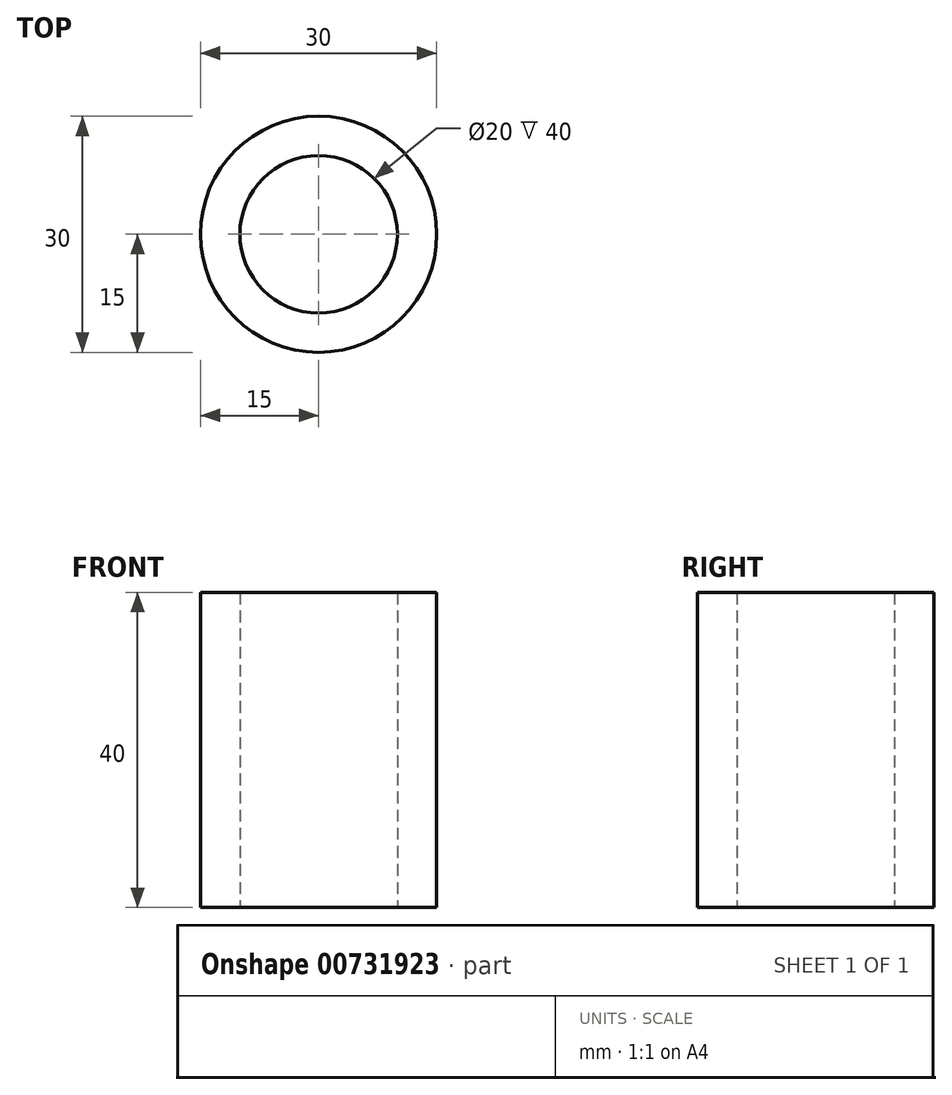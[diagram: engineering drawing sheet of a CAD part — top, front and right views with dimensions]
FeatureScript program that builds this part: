
annotation { "Feature Type Name" : "Feature", "Feature Type Description" : "" }
export const myFeature = defineFeature(function(context is Context, id is Id, definition is map)
    precondition{}
    {
        {
            var Q0;
            Q0=qCreatedBy(makeId("Top.planeOp"),FACE);
            var sketch = newSketch(context, id + "F0", { "sketchPlane" : qUnion([Q0])});
            skCircle(sketch, "E0", {"center": v(0, 0) * mm, "radius": 15 * mm});
            skCircle(sketch, "E1", {"center": v(0, 0) * mm, "radius": 10 * mm});
            skSolve(sketch);
        }
        {
            var Q0;
            Q0=makeQuery(id+"F0.imprint","IMPRINT",FACE,{"disambiguationData":[TD([[makeQuery(id+"F0.imprint","IMPRINT",EDGE,{"derivedFrom":sQuery(id+"F0.wireOp",EDGE,"E0")}),1.0]])]});
            extrude(context, id + "F1", {"entities" : qUnion([Q0]), "depth" : 40 * mm, "offsetDistance" : 25 * mm});
        }
        {
            var Q0;
            Q0=qCreatedBy(makeId("Top.planeOp"),FACE);
            var sketch = newSketch(context, id + "F2", { "sketchPlane" : qUnion([Q0])});
            skCircle(sketch, "E2", {"center": v(0, 0) * mm, "radius": 13.25 * mm});
            skSolve(sketch);
        }
        {
            var Q0;
            Q0=sQuery(id+"F2.wireOp",EDGE,"E2");
            extrude(context, id + "F3", {"bodyType" : ToolBodyType.SURFACE, "surfaceEntities" : qUnion([Q0]), "depth" : 25 * mm, "offsetDistance" : 25 * mm});
        }
    });
